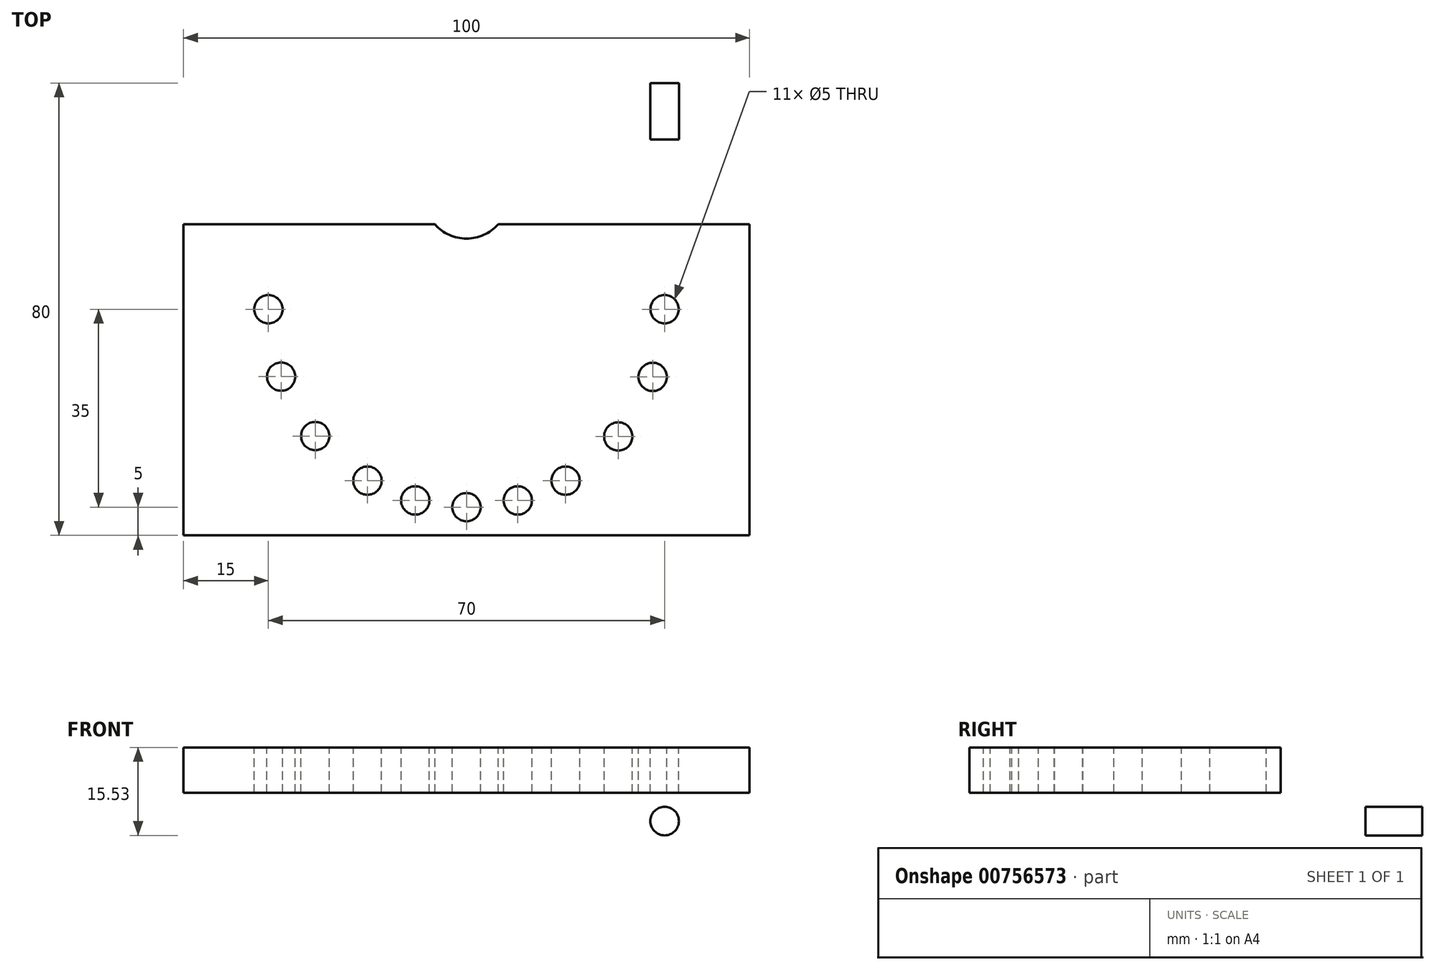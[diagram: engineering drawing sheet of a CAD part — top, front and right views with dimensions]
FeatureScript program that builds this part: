
annotation { "Feature Type Name" : "Feature", "Feature Type Description" : "" }
export const myFeature = defineFeature(function(context is Context, id is Id, definition is map)
    precondition{}
    {
        {
            var Q0;
            Q0=qCreatedBy(makeId("Top.planeOp"),FACE);
            var sketch = newSketch(context, id + "F0", { "sketchPlane" : qUnion([Q0])});
            skLineSegment(sketch, "E0.bottom", {"start": v(50, 40) * mm, "end": v(-50, 40) * mm});
            skLineSegment(sketch, "E0.top", {"start": v(50, -40) * mm, "end": v(-50, -40) * mm});
            skLineSegment(sketch, "E0.left", {"start": v(50, 40) * mm, "end": v(50, -40) * mm});
            skLineSegment(sketch, "E0.right", {"start": v(-50, 40) * mm, "end": v(-50, -40) * mm});
            skSolve(sketch);
        }
        {
            var Q0;
            Q0=makeQuery(id+"F0.imprint","IMPRINT",FACE,{"disambiguationData":[TD([[makeQuery(id+"F0.imprint","IMPRINT",EDGE,{"derivedFrom":sQuery(id+"F0.wireOp",EDGE,"E0.bottom")}),1.0]])]});
            extrude(context, id + "F1", {"entities" : qUnion([Q0]), "depth" : 8 * mm, "offsetDistance" : 25 * mm});
        }
        {
            var Q0;
            Q0=makeQuery(id+"F1.opExtrude","CAP_FACE",FACE,{"disambiguationData":[OSD([sQuery(id+"F0.wireOp",EDGE,"E0.bottom"),sQuery(id+"F0.wireOp",EDGE,"E0.top"),sQuery(id+"F0.wireOp",EDGE,"E0.left"),sQuery(id+"F0.wireOp",EDGE,"E0.right")])],"isStart":false});
            var sketch = newSketch(context, id + "F2", { "sketchPlane" : qUnion([Q0])});
            skCircle(sketch, "E1", {"center": v(-32.75, -11.92) * mm, "radius": 2.5 * mm});
            skCircle(sketch, "E2", {"center": v(-26.73, -22.43) * mm, "radius": 2.5 * mm});
            skCircle(sketch, "E3", {"center": v(-17.5, -30.31) * mm, "radius": 2.5 * mm});
            skCircle(sketch, "E4", {"center": v(0, -35) * mm, "radius": 2.5 * mm});
            skCircle(sketch, "E5", {"center": v(-35, 0) * mm, "radius": 2.5 * mm});
            skLineSegment(sketch, "E6", {"start": v(0, 0) * mm, "end": v(-35, 0) * mm, "construction": true});
            skLineSegment(sketch, "E7", {"start": v(0, 0) * mm, "end": v(-32.75, -11.92) * mm, "construction": true});
            skLineSegment(sketch, "E8", {"start": v(0, 0) * mm, "end": v(-26.73, -22.43) * mm, "construction": true});
            skLineSegment(sketch, "E9", {"start": v(0, 0) * mm, "end": v(-17.5, -30.31) * mm, "construction": true});
            skLineSegment(sketch, "E10", {"start": v(0, 0) * mm, "end": v(0, -35) * mm, "construction": true});
            skCircle(sketch, "E11", {"center": v(17.5, -30.31) * mm, "radius": 2.5 * mm});
            skCircle(sketch, "E12", {"center": v(26.81, -22.5) * mm, "radius": 2.5 * mm});
            skCircle(sketch, "E13", {"center": v(32.89, -11.97) * mm, "radius": 2.5 * mm});
            skCircle(sketch, "E14", {"center": v(35, 0) * mm, "radius": 2.5 * mm});
            skLineSegment(sketch, "E15", {"start": v(0, 0) * mm, "end": v(35, 0) * mm, "construction": true});
            skLineSegment(sketch, "E16", {"start": v(0, 0) * mm, "end": v(32.89, -11.97) * mm, "construction": true});
            skLineSegment(sketch, "E17", {"start": v(0, 0) * mm, "end": v(26.81, -22.5) * mm, "construction": true});
            skLineSegment(sketch, "E18", {"start": v(0, 0) * mm, "end": v(17.5, -30.31) * mm, "construction": true});
            skCircle(sketch, "E19", {"center": v(-9.06, -33.8) * mm, "radius": 2.5 * mm});
            skCircle(sketch, "E20", {"center": v(9.06, -33.8) * mm, "radius": 2.5 * mm});
            skLineSegment(sketch, "E21", {"start": v(0, 0) * mm, "end": v(-9.06, -33.8) * mm, "construction": true});
            skLineSegment(sketch, "E22", {"start": v(0, 0) * mm, "end": v(9.06, -33.8) * mm, "construction": true});
            skSolve(sketch);
        }
        {
            var Q0;
            Q0 = qSketchRegion(id + "F2", true);
            extrude(context, id + "F3", {"entities" : qUnion([Q0]), "operationType" : NewBodyOperationType.REMOVE, "oppositeDirection" : true, "depth" : 25 * mm, "offsetDistance" : 25 * mm});
        }
        {
            var Q0;
            Q0=makeQuery(id+"F1.opExtrude","CAP_FACE",FACE,{"disambiguationData":[OSD([sQuery(id+"F0.wireOp",EDGE,"E0.bottom"),sQuery(id+"F0.wireOp",EDGE,"E0.top"),sQuery(id+"F0.wireOp",EDGE,"E0.left"),sQuery(id+"F0.wireOp",EDGE,"E0.right")])],"isStart":true});
            var sketch = newSketch(context, id + "F4", { "sketchPlane" : qUnion([Q0])});
            skLineSegment(sketch, "E23.bottom", {"start": v(50, -40) * mm, "end": v(-50, -40) * mm});
            skLineSegment(sketch, "E23.top", {"start": v(50, -30) * mm, "end": v(-50, -30) * mm});
            skLineSegment(sketch, "E23.left", {"start": v(50, -40) * mm, "end": v(50, -30) * mm});
            skLineSegment(sketch, "E23.right", {"start": v(-50, -40) * mm, "end": v(-50, -30) * mm});
            skSolve(sketch);
        }
        {
            var Q0;
            Q0=makeQuery(id+"F4.imprint","IMPRINT",FACE,{"disambiguationData":[TD([[makeQuery(id+"F4.imprint","IMPRINT",EDGE,{"derivedFrom":sQuery(id+"F4.wireOp",EDGE,"E23.bottom")}),-1.0]])]});
            extrude(context, id + "F5", {"entities" : qUnion([Q0]), "operationType" : NewBodyOperationType.ADD, "depth" : 15 * mm, "offsetDistance" : 25 * mm});
        }
        {
            var Q0;
            Q0=makeQuery(id+"F5.boolean.opBoolean","MERGE",FACE,{"derivedFrom":[makeQuery(id+"F1.opExtrude","SWEPT_FACE",FACE,{"disambiguationData":[OSD([sQuery(id+"F0.wireOp",EDGE,"E0.bottom")])]}),makeQuery(id+"F5.opExtrude","SWEPT_FACE",FACE,{"disambiguationData":[OSD([sQuery(id+"F4.wireOp",EDGE,"E23.bottom")])]})]});
            var sketch = newSketch(context, id + "F6", { "sketchPlane" : qUnion([Q0])});
            skCircle(sketch, "E24", {"center": v(35, -5) * mm, "radius": 2.53 * mm});
            skLineSegment(sketch, "E25", {"start": v(0, -15) * mm, "end": v(0, 8) * mm, "construction": true});
            skCircle(sketch, "E26.MirrorC", {"center": v(-35, -5) * mm, "radius": 2.53 * mm});
            skSolve(sketch);
        }
        {
            var Q0;
            Q0=makeQuery(id+"F6.imprint","IMPRINT",FACE,{"disambiguationData":[TD([[makeQuery(id+"F6.imprint","IMPRINT",EDGE,{"derivedFrom":sQuery(id+"F6.wireOp",EDGE,"E24")}),1.0]])]});
            var Q1;
            Q1=makeQuery(id+"F6.imprint","IMPRINT",FACE,{"disambiguationData":[TD([[makeQuery(id+"F6.imprint","IMPRINT",EDGE,{"derivedFrom":sQuery(id+"F6.wireOp",EDGE,"E26.MirrorC")}),-1.0]])]});
            extrude(context, id + "F7", {"entities" : qUnion([Q0, Q1]), "operationType" : NewBodyOperationType.REMOVE, "oppositeDirection" : true, "depth" : 25 * mm, "offsetDistance" : 25 * mm});
        }
        {
            var Q0;
            Q0=makeQuery(id+"F1.opExtrude","CAP_FACE",FACE,{"disambiguationData":[OSD([sQuery(id+"F0.wireOp",EDGE,"E0.bottom"),sQuery(id+"F0.wireOp",EDGE,"E0.top"),sQuery(id+"F0.wireOp",EDGE,"E0.left"),sQuery(id+"F0.wireOp",EDGE,"E0.right")])],"isStart":false});
            var sketch = newSketch(context, id + "F8", { "sketchPlane" : qUnion([Q0])});
            skLineSegment(sketch, "E27", {"start": v(50, 20) * mm, "end": v(-50, 20) * mm, "construction": true});
            skCircle(sketch, "E28", {"center": v(0, 20) * mm, "radius": 7.5 * mm});
            skSolve(sketch);
        }
        {
            var Q0;
            Q0=makeQuery(id+"F8.imprint","IMPRINT",FACE,{"disambiguationData":[TD([[makeQuery(id+"F8.imprint","IMPRINT",EDGE,{"derivedFrom":sQuery(id+"F8.wireOp",EDGE,"E28")}),1.0]])]});
            var Q1;
            Q1=sQuery(id+"F8.wireOp",EDGE,"E28");
            extrude(context, id + "F9", {"entities" : qUnion([Q0]), "operationType" : NewBodyOperationType.REMOVE, "surfaceEntities" : qUnion([Q1]), "oppositeDirection" : true, "depth" : 25 * mm, "offsetDistance" : 25 * mm});
        }
    });
